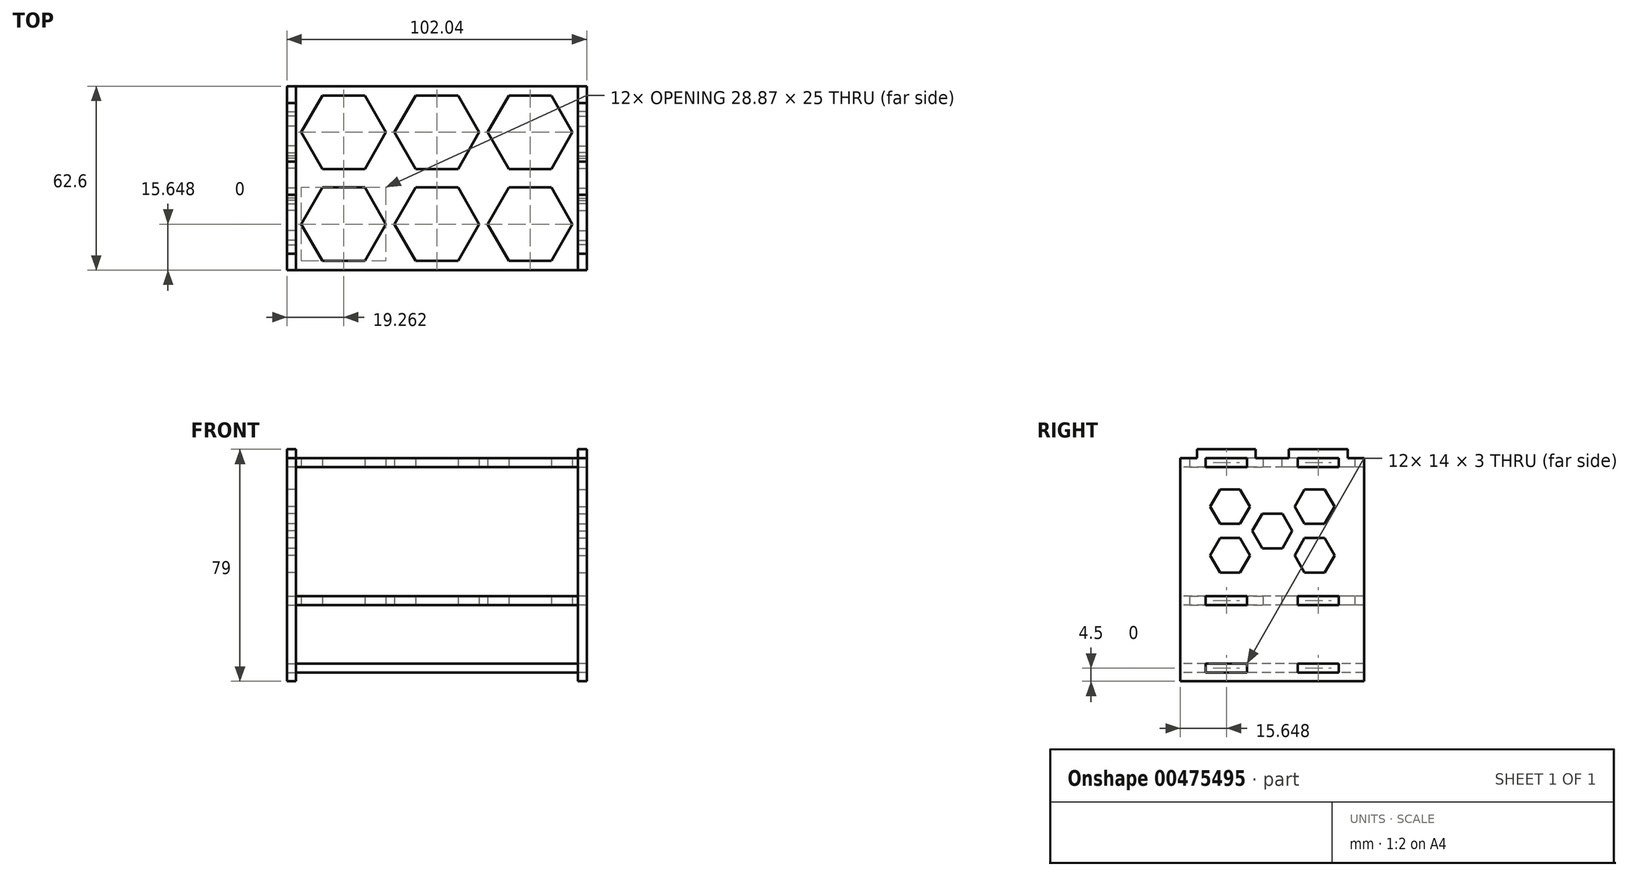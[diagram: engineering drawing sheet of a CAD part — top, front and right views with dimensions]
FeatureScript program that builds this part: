
annotation { "Feature Type Name" : "Feature", "Feature Type Description" : "" }
export const myFeature = defineFeature(function(context is Context, id is Id, definition is map)
    precondition{}
    {
        {
            assignVariable(context, id + "F0", {"name" : "x", "anyValue" : 3});
        }
        {
            var Q0;
            Q0=qCreatedBy(makeId("Top.planeOp"),FACE);
            var sketch = newSketch(context, id + "F1", { "sketchPlane" : qUnion([Q0])});
            skLineSegment(sketch, "E0.bottom", {"start": v(48.02, 31.3) * mm, "end": v(-48.02, 31.3) * mm});
            skLineSegment(sketch, "E0.top", {"start": v(48.02, -31.3) * mm, "end": v(-48.02, -31.3) * mm});
            skPoint(sketch, "E0.middle", {"position": v(0, 0) * mm});
            skCircle(sketch, "E1", {"center": v(-31.76, 15.65) * mm, "radius": 12.5 * mm, "construction": true});
            skCircle(sketch, "E2", {"center": v(0, 15.65) * mm, "radius": 12.5 * mm, "construction": true});
            skCircle(sketch, "E3", {"center": v(31.76, 15.65) * mm, "radius": 12.5 * mm, "construction": true});
            skPoint(sketch, "E4", {"position": v(-48.9, 0) * mm});
            skLineSegment(sketch, "E5", {"start": v(-51.02, 15.65) * mm, "end": v(51.02, 15.65) * mm, "construction": true});
            skLineSegment(sketch, "E6", {"start": v(-19.26, 15.65) * mm, "end": v(-12.5, 15.65) * mm, "construction": true});
            skLineSegment(sketch, "E7", {"start": v(12.5, 15.65) * mm, "end": v(19.26, 15.65) * mm, "construction": true});
            skLineSegment(sketch, "E8", {"start": v(-44.26, 15.65) * mm, "end": v(-51.02, 15.65) * mm, "construction": true});
            skLineSegment(sketch, "E9", {"start": v(44.26, 15.65) * mm, "end": v(51.02, 15.65) * mm, "construction": true});
            skLineSegment(sketch, "E10.bottom", {"start": v(-51.02, 8.65) * mm, "end": v(-48.02, 8.65) * mm});
            skLineSegment(sketch, "E10.top", {"start": v(-51.02, 22.65) * mm, "end": v(-48.02, 22.65) * mm});
            skLineSegment(sketch, "E10.left", {"start": v(-51.02, 8.65) * mm, "end": v(-51.02, 22.65) * mm});
            skLineSegment(sketch, "E11", {"start": v(-48.02, 31.3) * mm, "end": v(-48.02, 22.65) * mm});
            skLineSegment(sketch, "E12.MirrorCS", {"start": v(-51.02, -8.65) * mm, "end": v(-48.02, -8.65) * mm});
            skLineSegment(sketch, "E13.MirrorCS", {"start": v(-51.02, -22.65) * mm, "end": v(-48.02, -22.65) * mm});
            skLineSegment(sketch, "E14.MirrorCS", {"start": v(-51.02, -8.65) * mm, "end": v(-51.02, -22.65) * mm});
            skLineSegment(sketch, "E15.trimOffspring", {"start": v(-48.02, -22.65) * mm, "end": v(-48.02, -31.3) * mm});
            skPoint(sketch, "E16.MirrorCS.end.orphan", {"position": v(-48.02, -22.65) * mm});
            skPoint(sketch, "E16.MirrorCS.start.orphan", {"position": v(-48.02, -8.65) * mm});
            skLineSegment(sketch, "E17.trimOffspring", {"start": v(-48.02, 8.65) * mm, "end": v(-48.02, -8.65) * mm});
            skPoint(sketch, "E18.orphan", {"position": v(-63.77, 31.3) * mm});
            skPoint(sketch, "E19.orphan", {"position": v(-34.01, -31.3) * mm});
            skPoint(sketch, "E20.MirrorP", {"position": v(48.9, 0) * mm});
            skLineSegment(sketch, "E21.MirrorCS", {"start": v(51.02, 8.65) * mm, "end": v(51.02, 22.65) * mm});
            skLineSegment(sketch, "E22.MirrorCS", {"start": v(48.02, 8.65) * mm, "end": v(48.02, -8.65) * mm});
            skPoint(sketch, "E23.MirrorP", {"position": v(48.02, -8.65) * mm});
            skLineSegment(sketch, "E24.MirrorCS", {"start": v(51.02, 8.65) * mm, "end": v(48.02, 8.65) * mm});
            skLineSegment(sketch, "E25.MirrorCS", {"start": v(51.02, -8.65) * mm, "end": v(48.02, -8.65) * mm});
            skLineSegment(sketch, "E26.MirrorCS", {"start": v(51.02, -22.65) * mm, "end": v(48.02, -22.65) * mm});
            skPoint(sketch, "E27.MirrorP", {"position": v(48.02, -22.65) * mm});
            skLineSegment(sketch, "E28.MirrorCS", {"start": v(51.02, 22.65) * mm, "end": v(48.02, 22.65) * mm});
            skLineSegment(sketch, "E29.MirrorCS", {"start": v(51.02, -8.65) * mm, "end": v(51.02, -22.65) * mm});
            skLineSegment(sketch, "E30.MirrorCS", {"start": v(48.02, -22.65) * mm, "end": v(48.02, -31.3) * mm});
            skLineSegment(sketch, "E31.MirrorCS", {"start": v(48.02, 31.3) * mm, "end": v(48.02, 22.65) * mm});
            skPoint(sketch, "E32.orphan", {"position": v(34.01, 31.3) * mm});
            skPoint(sketch, "E33.orphan", {"position": v(63.77, -31.3) * mm});
            skLineSegment(sketch, "E34.0", {"start": v(-24.54, 28.15) * mm, "end": v(-17.32, 15.65) * mm});
            skLineSegment(sketch, "E34.1", {"start": v(-17.32, 15.65) * mm, "end": v(-24.54, 3.15) * mm});
            skLineSegment(sketch, "E34.2", {"start": v(-24.54, 3.15) * mm, "end": v(-38.97, 3.15) * mm});
            skLineSegment(sketch, "E34.3", {"start": v(-38.97, 3.15) * mm, "end": v(-46.2, 15.65) * mm});
            skLineSegment(sketch, "E34.4", {"start": v(-46.2, 15.65) * mm, "end": v(-38.97, 28.15) * mm});
            skLineSegment(sketch, "E34.5", {"start": v(-38.97, 28.15) * mm, "end": v(-24.54, 28.15) * mm});
            skPoint(sketch, "E34.0.midPoint", {"position": v(-20.93, 21.9) * mm});
            skLineSegment(sketch, "E35.0", {"start": v(7.22, 28.15) * mm, "end": v(14.43, 15.65) * mm});
            skLineSegment(sketch, "E35.1", {"start": v(14.43, 15.65) * mm, "end": v(7.22, 3.15) * mm});
            skLineSegment(sketch, "E35.2", {"start": v(7.22, 3.15) * mm, "end": v(-7.22, 3.15) * mm});
            skLineSegment(sketch, "E35.3", {"start": v(-7.22, 3.15) * mm, "end": v(-14.43, 15.65) * mm});
            skLineSegment(sketch, "E35.4", {"start": v(-14.43, 15.65) * mm, "end": v(-7.22, 28.15) * mm});
            skLineSegment(sketch, "E35.5", {"start": v(-7.22, 28.15) * mm, "end": v(7.22, 28.15) * mm});
            skPoint(sketch, "E35.0.midPoint", {"position": v(10.83, 21.9) * mm});
            skLineSegment(sketch, "E36.0", {"start": v(38.97, 28.15) * mm, "end": v(46.2, 15.65) * mm});
            skLineSegment(sketch, "E36.1", {"start": v(46.2, 15.65) * mm, "end": v(38.97, 3.15) * mm});
            skLineSegment(sketch, "E36.2", {"start": v(38.97, 3.15) * mm, "end": v(24.54, 3.15) * mm});
            skLineSegment(sketch, "E36.3", {"start": v(24.54, 3.15) * mm, "end": v(17.32, 15.65) * mm});
            skLineSegment(sketch, "E36.4", {"start": v(17.32, 15.65) * mm, "end": v(24.54, 28.15) * mm});
            skLineSegment(sketch, "E36.5", {"start": v(24.54, 28.15) * mm, "end": v(38.97, 28.15) * mm});
            skPoint(sketch, "E36.0.midPoint", {"position": v(42.58, 21.9) * mm});
            skLineSegment(sketch, "E37.MirrorCS", {"start": v(38.97, -3.15) * mm, "end": v(24.54, -3.15) * mm});
            skLineSegment(sketch, "E38.MirrorCS", {"start": v(24.54, -28.15) * mm, "end": v(38.97, -28.15) * mm});
            skLineSegment(sketch, "E39.MirrorCS", {"start": v(-24.54, -3.15) * mm, "end": v(-38.97, -3.15) * mm});
            skLineSegment(sketch, "E40.MirrorCS", {"start": v(-19.26, -15.65) * mm, "end": v(-12.5, -15.65) * mm, "construction": true});
            skLineSegment(sketch, "E41.MirrorCS", {"start": v(7.22, -3.15) * mm, "end": v(-7.22, -3.15) * mm});
            skLineSegment(sketch, "E42.MirrorCS", {"start": v(17.32, -15.65) * mm, "end": v(24.54, -28.15) * mm});
            skCircle(sketch, "E43.MirrorC", {"center": v(-31.76, -15.65) * mm, "radius": 12.5 * mm, "construction": true});
            skLineSegment(sketch, "E44.MirrorCS", {"start": v(7.22, -28.15) * mm, "end": v(14.43, -15.65) * mm});
            skLineSegment(sketch, "E45.MirrorCS", {"start": v(38.97, -28.15) * mm, "end": v(46.2, -15.65) * mm});
            skLineSegment(sketch, "E46.MirrorCS", {"start": v(-24.54, -28.15) * mm, "end": v(-17.32, -15.65) * mm});
            skCircle(sketch, "E47.MirrorC", {"center": v(0, -15.65) * mm, "radius": 12.5 * mm, "construction": true});
            skCircle(sketch, "E48.MirrorC", {"center": v(31.76, -15.65) * mm, "radius": 12.5 * mm, "construction": true});
            skLineSegment(sketch, "E49.MirrorCS", {"start": v(12.5, -15.65) * mm, "end": v(19.26, -15.65) * mm, "construction": true});
            skLineSegment(sketch, "E50.MirrorCS", {"start": v(-7.22, -3.15) * mm, "end": v(-14.43, -15.65) * mm});
            skLineSegment(sketch, "E51.MirrorCS", {"start": v(-7.22, -28.15) * mm, "end": v(7.22, -28.15) * mm});
            skLineSegment(sketch, "E52.MirrorCS", {"start": v(-46.2, -15.65) * mm, "end": v(-38.97, -28.15) * mm});
            skPoint(sketch, "E53.MirrorP", {"position": v(42.58, -21.9) * mm});
            skLineSegment(sketch, "E54.MirrorCS", {"start": v(-17.32, -15.65) * mm, "end": v(-24.54, -3.15) * mm});
            skLineSegment(sketch, "E55.MirrorCS", {"start": v(-38.97, -3.15) * mm, "end": v(-46.2, -15.65) * mm});
            skPoint(sketch, "E56.MirrorP", {"position": v(-20.93, -21.9) * mm});
            skPoint(sketch, "E57.MirrorP", {"position": v(10.83, -21.9) * mm});
            skLineSegment(sketch, "E58.MirrorCS", {"start": v(-38.97, -28.15) * mm, "end": v(-24.54, -28.15) * mm});
            skLineSegment(sketch, "E59.MirrorCS", {"start": v(-14.43, -15.65) * mm, "end": v(-7.22, -28.15) * mm});
            skLineSegment(sketch, "E60.MirrorCS", {"start": v(24.54, -3.15) * mm, "end": v(17.32, -15.65) * mm});
            skLineSegment(sketch, "E61.MirrorCS", {"start": v(14.43, -15.65) * mm, "end": v(7.22, -3.15) * mm});
            skLineSegment(sketch, "E62.MirrorCS", {"start": v(46.2, -15.65) * mm, "end": v(38.97, -3.15) * mm});
            skSolve(sketch);
        }
        {
            var Q0;
            Q0=makeQuery(id+"F1.imprint","IMPRINT",FACE,{"disambiguationData":[TD([[makeQuery(id+"F1.imprint","IMPRINT",EDGE,{"derivedFrom":sQuery(id+"F1.wireOp",EDGE,"E0.bottom")}),1.0]])]});
            extrude(context, id + "F2", {"entities" : qUnion([Q0]), "depth" : 50 * mm});
        }
        {
            var Q0;
            Q0=qSketchRegion(id+"F1",true);
            extrude(context, id + "F3", {"entities" : qUnion([Q0]), "operationType" : NewBodyOperationType.REMOVE, "depth" : (50 - getVariable(context, 'x')) * mm});
        }
        {
            var Q0;
            Q0=qSketchRegion(id+"F1",true);
            extrude(context, id + "F4", {"entities" : qUnion([Q0]), "depth" : (getVariable(context, 'x')) * mm});
        }
        {
            var Q0;
            Q0=makeQuery(id+"F1.imprint","IMPRINT",FACE,{"disambiguationData":[TD([[makeQuery(id+"F1.imprint","IMPRINT",EDGE,{"derivedFrom":sQuery(id+"F1.wireOp",EDGE,"E0.bottom")}),1.0]])]});
            var sketch = newSketch(context, id + "F5", { "sketchPlane" : qUnion([Q0])});
            skPoint(sketch, "E63", {"position": v(-48.02, -31.3) * mm});
            skLineSegment(sketch, "E64", {"start": v(-48.02, -31.3) * mm, "end": v(-48.02, -22.65) * mm});
            skLineSegment(sketch, "E65", {"start": v(-48.02, -22.65) * mm, "end": v(-51.02, -22.65) * mm});
            skLineSegment(sketch, "E66", {"start": v(-51.02, -22.65) * mm, "end": v(-51.02, -8.65) * mm});
            skLineSegment(sketch, "E67", {"start": v(-51.02, -8.65) * mm, "end": v(-48.02, -8.65) * mm});
            skLineSegment(sketch, "E68", {"start": v(-48.02, -8.65) * mm, "end": v(-48.02, 0) * mm});
            skLineSegment(sketch, "E69", {"start": v(-48.02, -31.3) * mm, "end": v(0, -31.3) * mm});
            skLineSegment(sketch, "E70.MirrorCS", {"start": v(48.02, -31.3) * mm, "end": v(48.02, -22.65) * mm});
            skLineSegment(sketch, "E71.MirrorCS", {"start": v(48.02, -22.65) * mm, "end": v(51.02, -22.65) * mm});
            skLineSegment(sketch, "E72.MirrorCS", {"start": v(51.02, -8.65) * mm, "end": v(48.02, -8.65) * mm});
            skLineSegment(sketch, "E73.MirrorCS", {"start": v(48.02, -8.65) * mm, "end": v(48.02, 0) * mm});
            skPoint(sketch, "E74.MirrorP", {"position": v(48.02, -31.3) * mm});
            skLineSegment(sketch, "E75.MirrorCS", {"start": v(48.02, -31.3) * mm, "end": v(0, -31.3) * mm});
            skLineSegment(sketch, "E76.MirrorCS", {"start": v(51.02, -22.65) * mm, "end": v(51.02, -8.65) * mm});
            skLineSegment(sketch, "E77.MirrorCS", {"start": v(51.02, 8.65) * mm, "end": v(48.02, 8.65) * mm});
            skLineSegment(sketch, "E78.MirrorCS", {"start": v(-48.02, 31.3) * mm, "end": v(-48.02, 22.65) * mm});
            skLineSegment(sketch, "E79.MirrorCS", {"start": v(-48.02, 22.65) * mm, "end": v(-51.02, 22.65) * mm});
            skLineSegment(sketch, "E80.MirrorCS", {"start": v(48.02, 22.65) * mm, "end": v(51.02, 22.65) * mm});
            skLineSegment(sketch, "E81.MirrorCS", {"start": v(-51.02, 8.65) * mm, "end": v(-48.02, 8.65) * mm});
            skLineSegment(sketch, "E82.MirrorCS", {"start": v(48.02, 31.3) * mm, "end": v(48.02, 22.65) * mm});
            skLineSegment(sketch, "E83.MirrorCS", {"start": v(48.02, 8.65) * mm, "end": v(48.02, 0) * mm});
            skLineSegment(sketch, "E84.MirrorCS", {"start": v(-48.02, 8.65) * mm, "end": v(-48.02, 0) * mm});
            skPoint(sketch, "E85.MirrorP", {"position": v(-48.02, 31.3) * mm});
            skPoint(sketch, "E86.MirrorP", {"position": v(48.02, 31.3) * mm});
            skLineSegment(sketch, "E87.MirrorCS", {"start": v(51.02, 22.65) * mm, "end": v(51.02, 8.65) * mm});
            skLineSegment(sketch, "E88.MirrorCS", {"start": v(48.02, 31.3) * mm, "end": v(0, 31.3) * mm});
            skLineSegment(sketch, "E89.MirrorCS", {"start": v(-51.02, 22.65) * mm, "end": v(-51.02, 8.65) * mm});
            skLineSegment(sketch, "E90.MirrorCS", {"start": v(-48.02, 31.3) * mm, "end": v(0, 31.3) * mm});
            skSolve(sketch);
        }
        {
            var Q0;
            Q0=qSketchRegion(id+"F5",true);
            extrude(context, id + "F6", {"entities" : qUnion([Q0]), "oppositeDirection" : true, "depth" : 23 * mm});
        }
        {
            var Q0;
            Q0=qSketchRegion(id+"F5",true);
            extrude(context, id + "F7", {"entities" : qUnion([Q0]), "operationType" : NewBodyOperationType.REMOVE, "oppositeDirection" : true, "depth" : (23 - getVariable(context, 'x')) * mm});
        }
        {
            var Q0;
            Q0=makeQuery(id+"F4.opExtrude","SWEPT_FACE",FACE,{"disambiguationData":[OSD([sQuery(id+"F1.wireOp",EDGE,"E14.MirrorCS")])]});
            var sketch = newSketch(context, id + "F8", { "sketchPlane" : qUnion([Q0])});
            skLineSegment(sketch, "E91", {"start": v(31.3, -23) * mm, "end": v(31.3, 50) * mm});
            skLineSegment(sketch, "E92", {"start": v(31.3, 50) * mm, "end": v(25.65, 50) * mm});
            skLineSegment(sketch, "E93", {"start": v(25.65, 50) * mm, "end": v(25.65, 53) * mm});
            skLineSegment(sketch, "E94", {"start": v(25.65, 53) * mm, "end": v(5.65, 53) * mm});
            skLineSegment(sketch, "E95", {"start": v(5.65, 53) * mm, "end": v(5.65, 50) * mm});
            skLineSegment(sketch, "E96", {"start": v(5.65, 50) * mm, "end": v(0, 50) * mm});
            skLineSegment(sketch, "E97", {"start": v(31.3, -23) * mm, "end": v(31.3, -26) * mm});
            skLineSegment(sketch, "E98", {"start": v(31.3, -26) * mm, "end": v(0, -26) * mm});
            skLineSegment(sketch, "E99.bottom", {"start": v(8.65, -23) * mm, "end": v(22.65, -23) * mm});
            skLineSegment(sketch, "E99.top", {"start": v(8.65, -20) * mm, "end": v(22.65, -20) * mm});
            skLineSegment(sketch, "E99.left", {"start": v(8.65, -23) * mm, "end": v(8.65, -20) * mm});
            skLineSegment(sketch, "E99.right", {"start": v(22.65, -23) * mm, "end": v(22.65, -20) * mm});
            skLineSegment(sketch, "E100.bottom", {"start": v(8.65, 0) * mm, "end": v(22.65, 0) * mm});
            skLineSegment(sketch, "E100.top", {"start": v(8.65, 3) * mm, "end": v(22.65, 3) * mm});
            skLineSegment(sketch, "E100.left", {"start": v(8.65, 0) * mm, "end": v(8.65, 3) * mm});
            skLineSegment(sketch, "E100.right", {"start": v(22.65, 0) * mm, "end": v(22.65, 3) * mm});
            skLineSegment(sketch, "E101.bottom", {"start": v(8.65, 47) * mm, "end": v(22.65, 47) * mm});
            skLineSegment(sketch, "E101.top", {"start": v(8.65, 50) * mm, "end": v(22.65, 50) * mm});
            skLineSegment(sketch, "E101.left", {"start": v(8.65, 47) * mm, "end": v(8.65, 50) * mm});
            skLineSegment(sketch, "E101.right", {"start": v(22.65, 47) * mm, "end": v(22.65, 50) * mm});
            skLineSegment(sketch, "E102.MirrorCS", {"start": v(-22.65, 0) * mm, "end": v(-22.65, 3) * mm});
            skLineSegment(sketch, "E103.MirrorCS", {"start": v(-8.65, 0) * mm, "end": v(-8.65, 3) * mm});
            skLineSegment(sketch, "E104.MirrorCS", {"start": v(-8.65, 0) * mm, "end": v(-22.65, 0) * mm});
            skLineSegment(sketch, "E105.MirrorCS", {"start": v(-8.65, 47) * mm, "end": v(-8.65, 50) * mm});
            skLineSegment(sketch, "E106.MirrorCS", {"start": v(-5.65, 53) * mm, "end": v(-5.65, 50) * mm});
            skLineSegment(sketch, "E107.MirrorCS", {"start": v(-8.65, -23) * mm, "end": v(-8.65, -20) * mm});
            skLineSegment(sketch, "E108.MirrorCS", {"start": v(-22.65, -23) * mm, "end": v(-22.65, -20) * mm});
            skLineSegment(sketch, "E109.MirrorCS", {"start": v(-31.3, 50) * mm, "end": v(-25.65, 50) * mm});
            skLineSegment(sketch, "E110.MirrorCS", {"start": v(-25.65, 50) * mm, "end": v(-25.65, 53) * mm});
            skLineSegment(sketch, "E111.MirrorCS", {"start": v(-22.65, 47) * mm, "end": v(-22.65, 50) * mm});
            skLineSegment(sketch, "E112.MirrorCS", {"start": v(-31.3, -23) * mm, "end": v(-31.3, -26) * mm});
            skLineSegment(sketch, "E113.MirrorCS", {"start": v(-25.65, 53) * mm, "end": v(-5.65, 53) * mm});
            skLineSegment(sketch, "E114.MirrorCS", {"start": v(-5.65, 50) * mm, "end": v(0, 50) * mm});
            skLineSegment(sketch, "E115.MirrorCS", {"start": v(-8.65, -20) * mm, "end": v(-22.65, -20) * mm});
            skLineSegment(sketch, "E116.MirrorCS", {"start": v(-8.65, 47) * mm, "end": v(-22.65, 47) * mm});
            skLineSegment(sketch, "E117.MirrorCS", {"start": v(-31.3, -23) * mm, "end": v(-31.3, 50) * mm});
            skLineSegment(sketch, "E118.MirrorCS", {"start": v(-8.65, -23) * mm, "end": v(-22.65, -23) * mm});
            skLineSegment(sketch, "E119.MirrorCS", {"start": v(-8.65, 3) * mm, "end": v(-22.65, 3) * mm});
            skLineSegment(sketch, "E120.MirrorCS", {"start": v(-31.3, -26) * mm, "end": v(0, -26) * mm});
            skLineSegment(sketch, "E121.MirrorCS", {"start": v(-8.65, 50) * mm, "end": v(-22.65, 50) * mm});
            skCircle(sketch, "E122.cCircle", {"center": v(0, 25.17) * mm, "radius": 6.8 * mm, "construction": true});
            skLineSegment(sketch, "E122.0", {"start": v(6.8, 25.17) * mm, "end": v(3.4, 19.29) * mm});
            skLineSegment(sketch, "E122.1", {"start": v(3.4, 19.29) * mm, "end": v(-3.4, 19.29) * mm});
            skLineSegment(sketch, "E122.2", {"start": v(-3.4, 19.29) * mm, "end": v(-6.8, 25.17) * mm});
            skLineSegment(sketch, "E122.3", {"start": v(-6.8, 25.17) * mm, "end": v(-3.4, 31.06) * mm});
            skLineSegment(sketch, "E122.4", {"start": v(-3.4, 31.06) * mm, "end": v(3.4, 31.06) * mm});
            skLineSegment(sketch, "E122.5", {"start": v(3.4, 31.06) * mm, "end": v(6.8, 25.17) * mm});
            skCircle(sketch, "E123.cCircle", {"center": v(-14.38, 33.48) * mm, "radius": 6.8 * mm, "construction": true});
            skLineSegment(sketch, "E123.0", {"start": v(-7.59, 33.48) * mm, "end": v(-10.99, 27.6) * mm});
            skLineSegment(sketch, "E123.1", {"start": v(-10.99, 27.6) * mm, "end": v(-17.78, 27.6) * mm});
            skLineSegment(sketch, "E123.2", {"start": v(-17.78, 27.6) * mm, "end": v(-21.18, 33.48) * mm});
            skLineSegment(sketch, "E123.3", {"start": v(-21.18, 33.48) * mm, "end": v(-17.78, 39.36) * mm});
            skLineSegment(sketch, "E123.4", {"start": v(-17.78, 39.36) * mm, "end": v(-10.99, 39.36) * mm});
            skLineSegment(sketch, "E123.5", {"start": v(-10.99, 39.36) * mm, "end": v(-7.59, 33.48) * mm});
            skCircle(sketch, "E124.cCircle", {"center": v(14.38, 33.48) * mm, "radius": 6.8 * mm, "construction": true});
            skLineSegment(sketch, "E124.0", {"start": v(21.18, 33.48) * mm, "end": v(17.78, 27.6) * mm});
            skLineSegment(sketch, "E124.1", {"start": v(17.78, 27.6) * mm, "end": v(10.99, 27.6) * mm});
            skLineSegment(sketch, "E124.2", {"start": v(10.99, 27.6) * mm, "end": v(7.59, 33.48) * mm});
            skLineSegment(sketch, "E124.3", {"start": v(7.59, 33.48) * mm, "end": v(10.99, 39.36) * mm});
            skLineSegment(sketch, "E124.4", {"start": v(10.99, 39.36) * mm, "end": v(17.78, 39.36) * mm});
            skLineSegment(sketch, "E124.5", {"start": v(17.78, 39.36) * mm, "end": v(21.18, 33.48) * mm});
            skCircle(sketch, "E125.cCircle", {"center": v(-14.38, 16.87) * mm, "radius": 6.8 * mm, "construction": true});
            skLineSegment(sketch, "E125.0", {"start": v(-7.59, 16.87) * mm, "end": v(-10.99, 10.98) * mm});
            skLineSegment(sketch, "E125.1", {"start": v(-10.99, 10.98) * mm, "end": v(-17.78, 10.98) * mm});
            skLineSegment(sketch, "E125.2", {"start": v(-17.78, 10.98) * mm, "end": v(-21.18, 16.87) * mm});
            skLineSegment(sketch, "E125.3", {"start": v(-21.18, 16.87) * mm, "end": v(-17.78, 22.75) * mm});
            skLineSegment(sketch, "E125.4", {"start": v(-17.78, 22.75) * mm, "end": v(-10.99, 22.75) * mm});
            skLineSegment(sketch, "E125.5", {"start": v(-10.99, 22.75) * mm, "end": v(-7.59, 16.87) * mm});
            skCircle(sketch, "E126.cCircle", {"center": v(14.38, 16.87) * mm, "radius": 6.8 * mm, "construction": true});
            skLineSegment(sketch, "E126.0", {"start": v(21.18, 16.87) * mm, "end": v(17.78, 10.98) * mm});
            skLineSegment(sketch, "E126.1", {"start": v(17.78, 10.98) * mm, "end": v(10.99, 10.98) * mm});
            skLineSegment(sketch, "E126.2", {"start": v(10.99, 10.98) * mm, "end": v(7.59, 16.87) * mm});
            skLineSegment(sketch, "E126.3", {"start": v(7.59, 16.87) * mm, "end": v(10.99, 22.75) * mm});
            skLineSegment(sketch, "E126.4", {"start": v(10.99, 22.75) * mm, "end": v(17.78, 22.75) * mm});
            skLineSegment(sketch, "E126.5", {"start": v(17.78, 22.75) * mm, "end": v(21.18, 16.87) * mm});
            skLineSegment(sketch, "E127", {"start": v(-17.78, 39.36) * mm, "end": v(21.18, 16.87) * mm, "construction": true});
            skLineSegment(sketch, "E128", {"start": v(-21.18, 16.87) * mm, "end": v(17.78, 39.36) * mm, "construction": true});
            skSolve(sketch);
        }
        {
            var Q0;
            Q0=qSketchRegion(id+"F8",true);
            extrude(context, id + "F9", {"entities" : qUnion([Q0]), "oppositeDirection" : true, "depth" : (getVariable(context, 'x')) * mm});
        }
        {
            var Q0;
            Q0=makeQuery(id+"F9.opExtrude","SWEPT_BODY",BODY,{"disambiguationData":[OSD([sQuery(id+"F8.wireOp",EDGE,"E91"),sQuery(id+"F8.wireOp",EDGE,"E92"),sQuery(id+"F8.wireOp",EDGE,"E93"),sQuery(id+"F8.wireOp",EDGE,"E94"),sQuery(id+"F8.wireOp",EDGE,"E95"),sQuery(id+"F8.wireOp",EDGE,"E96"),sQuery(id+"F8.wireOp",EDGE,"E97"),sQuery(id+"F8.wireOp",EDGE,"E98"),sQuery(id+"F8.wireOp",EDGE,"E99.bottom"),sQuery(id+"F8.wireOp",EDGE,"E99.top"),sQuery(id+"F8.wireOp",EDGE,"E99.left"),sQuery(id+"F8.wireOp",EDGE,"E99.right"),sQuery(id+"F8.wireOp",EDGE,"E100.bottom"),sQuery(id+"F8.wireOp",EDGE,"E100.top"),sQuery(id+"F8.wireOp",EDGE,"E100.left"),sQuery(id+"F8.wireOp",EDGE,"E100.right"),sQuery(id+"F8.wireOp",EDGE,"E101.bottom"),sQuery(id+"F8.wireOp",EDGE,"E101.top"),sQuery(id+"F8.wireOp",EDGE,"E101.left"),sQuery(id+"F8.wireOp",EDGE,"E101.right"),sQuery(id+"F8.wireOp",EDGE,"E102.MirrorCS"),sQuery(id+"F8.wireOp",EDGE,"E103.MirrorCS"),sQuery(id+"F8.wireOp",EDGE,"E104.MirrorCS"),sQuery(id+"F8.wireOp",EDGE,"E105.MirrorCS"),sQuery(id+"F8.wireOp",EDGE,"E106.MirrorCS"),sQuery(id+"F8.wireOp",EDGE,"E107.MirrorCS"),sQuery(id+"F8.wireOp",EDGE,"E108.MirrorCS"),sQuery(id+"F8.wireOp",EDGE,"E109.MirrorCS"),sQuery(id+"F8.wireOp",EDGE,"E110.MirrorCS"),sQuery(id+"F8.wireOp",EDGE,"E111.MirrorCS"),sQuery(id+"F8.wireOp",EDGE,"E112.MirrorCS"),sQuery(id+"F8.wireOp",EDGE,"E113.MirrorCS"),sQuery(id+"F8.wireOp",EDGE,"E114.MirrorCS"),sQuery(id+"F8.wireOp",EDGE,"E115.MirrorCS"),sQuery(id+"F8.wireOp",EDGE,"E116.MirrorCS"),sQuery(id+"F8.wireOp",EDGE,"E117.MirrorCS"),sQuery(id+"F8.wireOp",EDGE,"E118.MirrorCS"),sQuery(id+"F8.wireOp",EDGE,"E119.MirrorCS"),sQuery(id+"F8.wireOp",EDGE,"E120.MirrorCS"),sQuery(id+"F8.wireOp",EDGE,"E121.MirrorCS"),sQuery(id+"F8.wireOp",EDGE,"E122.0"),sQuery(id+"F8.wireOp",EDGE,"E122.1"),sQuery(id+"F8.wireOp",EDGE,"E122.2"),sQuery(id+"F8.wireOp",EDGE,"E122.3"),sQuery(id+"F8.wireOp",EDGE,"E122.4"),sQuery(id+"F8.wireOp",EDGE,"E122.5"),sQuery(id+"F8.wireOp",EDGE,"E123.0"),sQuery(id+"F8.wireOp",EDGE,"E123.1"),sQuery(id+"F8.wireOp",EDGE,"E123.2"),sQuery(id+"F8.wireOp",EDGE,"E123.3"),sQuery(id+"F8.wireOp",EDGE,"E123.4"),sQuery(id+"F8.wireOp",EDGE,"E123.5"),sQuery(id+"F8.wireOp",EDGE,"E124.0"),sQuery(id+"F8.wireOp",EDGE,"E124.1"),sQuery(id+"F8.wireOp",EDGE,"E124.2"),sQuery(id+"F8.wireOp",EDGE,"E124.3"),sQuery(id+"F8.wireOp",EDGE,"E124.4"),sQuery(id+"F8.wireOp",EDGE,"E124.5"),sQuery(id+"F8.wireOp",EDGE,"E125.0"),sQuery(id+"F8.wireOp",EDGE,"E125.1"),sQuery(id+"F8.wireOp",EDGE,"E125.2"),sQuery(id+"F8.wireOp",EDGE,"E125.3"),sQuery(id+"F8.wireOp",EDGE,"E125.4"),sQuery(id+"F8.wireOp",EDGE,"E125.5"),sQuery(id+"F8.wireOp",EDGE,"E126.0"),sQuery(id+"F8.wireOp",EDGE,"E126.1"),sQuery(id+"F8.wireOp",EDGE,"E126.2"),sQuery(id+"F8.wireOp",EDGE,"E126.3"),sQuery(id+"F8.wireOp",EDGE,"E126.4"),sQuery(id+"F8.wireOp",EDGE,"E126.5")])]});
            var Q1;
            Q1=qCreatedBy(makeId("Right.planeOp"),FACE);
            mirror(context, id + "F10", {"entities" : qUnion([Q0]), "mirrorPlane" : qUnion([Q1])});
        }
    });
